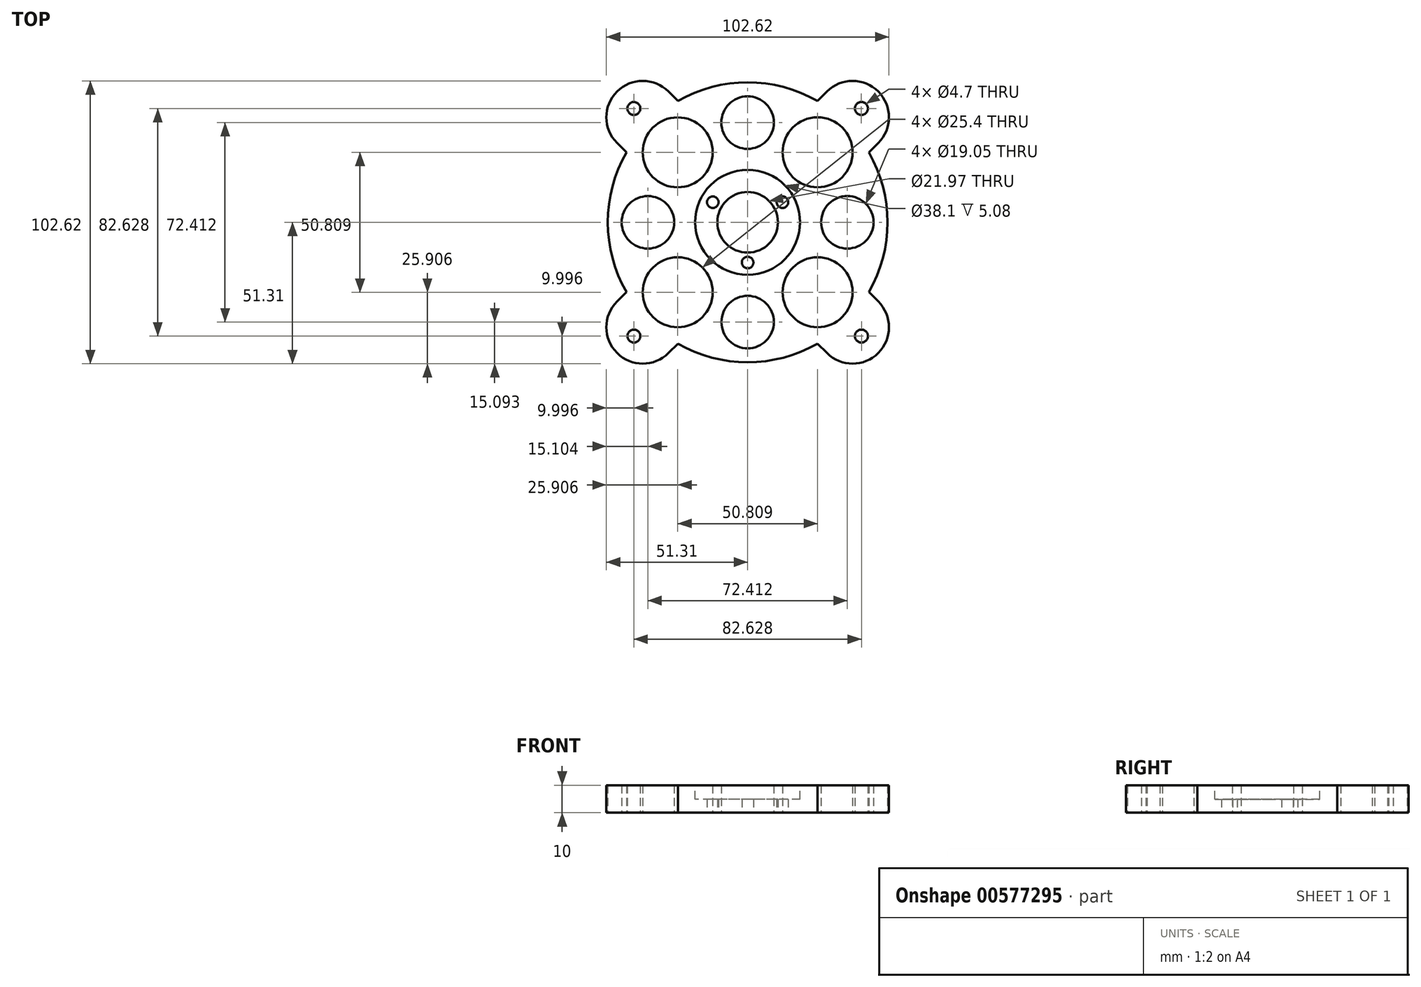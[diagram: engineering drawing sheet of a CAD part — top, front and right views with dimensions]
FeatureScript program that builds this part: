
annotation { "Feature Type Name" : "Feature", "Feature Type Description" : "" }
export const myFeature = defineFeature(function(context is Context, id is Id, definition is map)
    precondition{}
    {
        {
            var Q0;
            Q0=qCreatedBy(makeId("Top.planeOp"),FACE);
            var sketch = newSketch(context, id + "F0", { "sketchPlane" : qUnion([Q0])});
            skArc(sketch, "E0", {"start": v(-44.03, 25.35) * mm, "mid": v(-50.8, 0) * mm, "end": v(-44.03, -25.35) * mm});
            skCircle(sketch, "E1", {"center": v(0, 0) * mm, "radius": 10.99 * mm});
            skCircle(sketch, "E2.1.0", {"center": v(0, -14.6) * mm, "radius": 2.1 * mm});
            skCircle(sketch, "E3", {"center": v(0, 36.2) * mm, "radius": 9.53 * mm});
            skPoint(sketch, "E3.first.point", {"position": v(-0.68, 45.7) * mm});
            skPoint(sketch, "E3.second.point", {"position": v(3.54, 27.35) * mm});
            skPoint(sketch, "E3.third.point", {"position": v(-5.5, 28.41) * mm});
            skCircle(sketch, "E4.1.0", {"center": v(36.2, 0) * mm, "radius": 9.53 * mm});
            skCircle(sketch, "E4.2.0", {"center": v(0, -36.22) * mm, "radius": 9.53 * mm});
            skCircle(sketch, "E4.3.0", {"center": v(-36.2, -0.02) * mm, "radius": 9.53 * mm});
            skPoint(sketch, "E4.center", {"position": v(0, -0.01) * mm});
            skLineSegment(sketch, "E4.anchor1", {"start": v(0, -0.01) * mm, "end": v(0, 36.2) * mm, "construction": true});
            skLineSegment(sketch, "E4.anchor2", {"start": v(0, -0.01) * mm, "end": v(-36.2, -0.02) * mm, "construction": true});
            skCircle(sketch, "E5", {"center": v(-25.4, 25.38) * mm, "radius": 12.7 * mm});
            skPoint(sketch, "E5.first.point", {"position": v(-26.12, 38.06) * mm});
            skPoint(sketch, "E5.second.point", {"position": v(-13.39, 29.49) * mm});
            skPoint(sketch, "E5.third.point", {"position": v(-34.89, 16.94) * mm});
            skCircle(sketch, "E6.1.0", {"center": v(-25.38, -25.4) * mm, "radius": 12.7 * mm});
            skCircle(sketch, "E6.2.0", {"center": v(25.4, -25.38) * mm, "radius": 12.7 * mm});
            skCircle(sketch, "E6.3.0", {"center": v(25.38, 25.4) * mm, "radius": 12.7 * mm});
            skCircle(sketch, "E7", {"center": v(-41.31, 41.3) * mm, "radius": 2.35 * mm});
            skPoint(sketch, "E7.first.point", {"position": v(-40.3, 43.43) * mm});
            skPoint(sketch, "E7.second.point", {"position": v(-39.05, 40.68) * mm});
            skPoint(sketch, "E7.third.point", {"position": v(-43.32, 40.09) * mm});
            skCircle(sketch, "E8.1.0", {"center": v(-41.3, -41.31) * mm, "radius": 2.35 * mm});
            skCircle(sketch, "E8.2.0", {"center": v(41.31, -41.3) * mm, "radius": 2.35 * mm});
            skCircle(sketch, "E8.3.0", {"center": v(41.3, 41.31) * mm, "radius": 2.35 * mm});
            skPoint(sketch, "E9.first.point", {"position": v(-51.04, 35.8) * mm});
            skPoint(sketch, "E9.second.point", {"position": v(-48.29, 46.41) * mm});
            skPoint(sketch, "E9.third.point", {"position": v(-39.7, 51.15) * mm});
            skLineSegment(sketch, "E10", {"start": v(-44.03, 25.35) * mm, "end": v(-47.44, 28.76) * mm});
            skLineSegment(sketch, "E11", {"start": v(0, 0) * mm, "end": v(-56.16, 56.16) * mm, "construction": true});
            skArc(sketch, "E12.trimOffspring", {"start": v(-28.76, 47.44) * mm, "mid": v(-47.44, 47.44) * mm, "end": v(-47.44, 28.76) * mm});
            skLineSegment(sketch, "E13", {"start": v(-28.76, 47.44) * mm, "end": v(-25.35, 44.03) * mm});
            skArc(sketch, "E14.1.0", {"start": v(-47.44, -28.76) * mm, "mid": v(-47.44, -47.44) * mm, "end": v(-28.76, -47.44) * mm});
            skLineSegment(sketch, "E14.1.1", {"start": v(-47.44, -28.76) * mm, "end": v(-44.03, -25.35) * mm});
            skLineSegment(sketch, "E14.1.2", {"start": v(-25.35, -44.03) * mm, "end": v(-28.76, -47.44) * mm});
            skArc(sketch, "E14.2.0", {"start": v(28.76, -47.44) * mm, "mid": v(47.44, -47.44) * mm, "end": v(47.44, -28.76) * mm});
            skLineSegment(sketch, "E14.2.1", {"start": v(28.76, -47.44) * mm, "end": v(25.35, -44.03) * mm});
            skLineSegment(sketch, "E14.2.2", {"start": v(44.03, -25.35) * mm, "end": v(47.44, -28.76) * mm});
            skArc(sketch, "E14.3.0", {"start": v(47.44, 28.76) * mm, "mid": v(47.44, 47.44) * mm, "end": v(28.76, 47.44) * mm});
            skLineSegment(sketch, "E14.3.1", {"start": v(47.44, 28.76) * mm, "end": v(44.03, 25.35) * mm});
            skLineSegment(sketch, "E14.3.2", {"start": v(25.35, 44.03) * mm, "end": v(28.76, 47.44) * mm});
            skArc(sketch, "E15.trimOffspring", {"start": v(25.35, 44.03) * mm, "mid": v(0, 50.8) * mm, "end": v(-25.35, 44.03) * mm});
            skArc(sketch, "E16.trimOffspring", {"start": v(44.03, -25.35) * mm, "mid": v(50.8, 0) * mm, "end": v(44.03, 25.35) * mm});
            skArc(sketch, "E17.trimOffspring", {"start": v(-25.35, -44.03) * mm, "mid": v(0, -50.8) * mm, "end": v(25.35, -44.03) * mm});
            skCircle(sketch, "E18.1.0", {"center": v(12.65, 7.3) * mm, "radius": 2.1 * mm});
            skCircle(sketch, "E18.2.0", {"center": v(-12.65, 7.3) * mm, "radius": 2.1 * mm});
            skSolve(sketch);
        }
        {
            var Q0;
            Q0 = qSketchRegion(id + "F0", true);
            extrude(context, id + "F1", {"entities" : qUnion([Q0]), "endBound" : BoundingType.SYMMETRIC, "depth" : 10 * mm, "offsetDistance" : 25.4 * mm});
        }
        {
            var Q0;
            Q0=makeQuery(id+"F1.opExtrude","CAP_FACE",FACE,{"disambiguationData":[OSD([sQuery(id+"F0.wireOp",EDGE,"E0"),sQuery(id+"F0.wireOp",EDGE,"E1"),sQuery(id+"F0.wireOp",EDGE,"86b9931d-2bda-4839-9692-78589d5baaec"),sQuery(id+"F0.wireOp",EDGE,"E2.1.0"),sQuery(id+"F0.wireOp",EDGE,"E2.2.0"),sQuery(id+"F0.wireOp",EDGE,"E3"),sQuery(id+"F0.wireOp",EDGE,"E4.1.0"),sQuery(id+"F0.wireOp",EDGE,"E4.2.0"),sQuery(id+"F0.wireOp",EDGE,"E4.3.0"),sQuery(id+"F0.wireOp",EDGE,"E5"),sQuery(id+"F0.wireOp",EDGE,"E6.1.0"),sQuery(id+"F0.wireOp",EDGE,"E6.2.0"),sQuery(id+"F0.wireOp",EDGE,"E6.3.0"),sQuery(id+"F0.wireOp",EDGE,"E7"),sQuery(id+"F0.wireOp",EDGE,"E8.1.0"),sQuery(id+"F0.wireOp",EDGE,"E8.2.0"),sQuery(id+"F0.wireOp",EDGE,"E8.3.0"),sQuery(id+"F0.wireOp",EDGE,"E10"),sQuery(id+"F0.wireOp",EDGE,"E12.trimOffspring"),sQuery(id+"F0.wireOp",EDGE,"E13"),sQuery(id+"F0.wireOp",EDGE,"E14.1.0"),sQuery(id+"F0.wireOp",EDGE,"E14.1.1"),sQuery(id+"F0.wireOp",EDGE,"E14.1.2"),sQuery(id+"F0.wireOp",EDGE,"E14.2.0"),sQuery(id+"F0.wireOp",EDGE,"E14.2.1"),sQuery(id+"F0.wireOp",EDGE,"E14.2.2"),sQuery(id+"F0.wireOp",EDGE,"E14.3.0"),sQuery(id+"F0.wireOp",EDGE,"E14.3.1"),sQuery(id+"F0.wireOp",EDGE,"E14.3.2"),sQuery(id+"F0.wireOp",EDGE,"E15.trimOffspring"),sQuery(id+"F0.wireOp",EDGE,"E16.trimOffspring"),sQuery(id+"F0.wireOp",EDGE,"E17.trimOffspring")])],"isStart":false});
            var sketch = newSketch(context, id + "F2", { "sketchPlane" : qUnion([Q0])});
            skCircle(sketch, "E19", {"center": v(0, 0) * mm, "radius": 19.05 * mm});
            skSolve(sketch);
        }
        {
            var Q0;
            Q0 = qSketchRegion(id + "F2", true);
            extrude(context, id + "F3", {"entities" : qUnion([Q0]), "operationType" : NewBodyOperationType.REMOVE, "oppositeDirection" : true, "depth" : 5.08 * mm, "offsetDistance" : 25.4 * mm});
        }
    });
